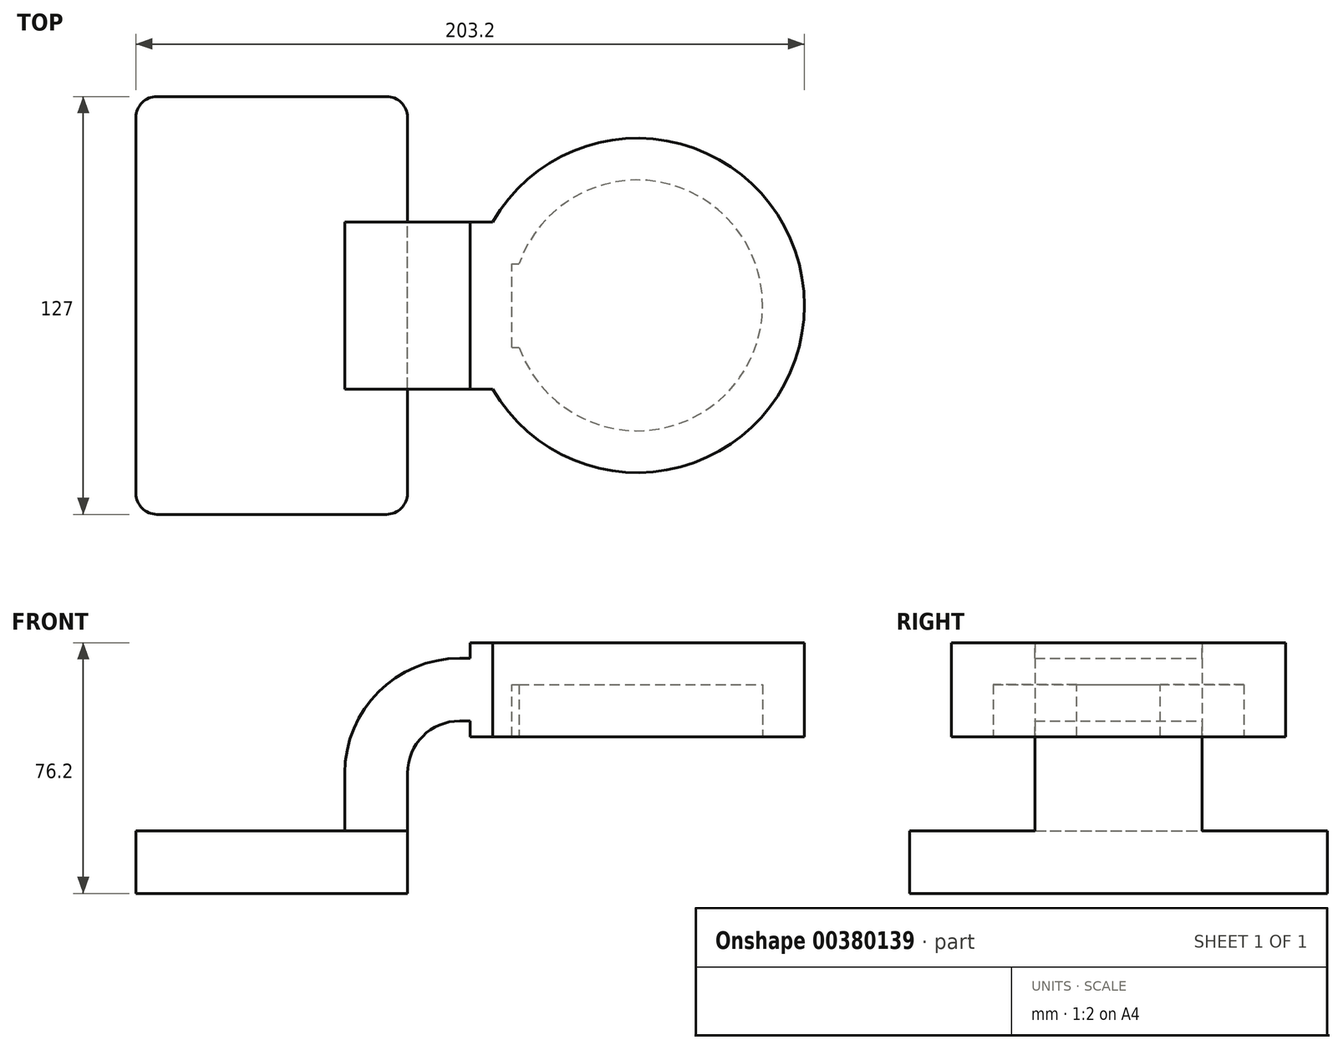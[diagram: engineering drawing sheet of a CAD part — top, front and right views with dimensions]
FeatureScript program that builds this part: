
annotation { "Feature Type Name" : "Feature", "Feature Type Description" : "" }
export const myFeature = defineFeature(function(context is Context, id is Id, definition is map)
    precondition{}
    {
        {
            var Q0;
            Q0=qCreatedBy(makeId("Front.planeOp"),FACE);
            var sketch = newSketch(context, id + "F0", { "sketchPlane" : qUnion([Q0])});
            skLineSegment(sketch, "E0.bottom", {"start": v(-41.28, 9.52) * mm, "end": v(41.27, 9.53) * mm});
            skLineSegment(sketch, "E0.top", {"start": v(-41.28, -9.53) * mm, "end": v(41.28, -9.53) * mm});
            skLineSegment(sketch, "E0.left", {"start": v(-41.28, 9.52) * mm, "end": v(-41.28, -9.53) * mm});
            skLineSegment(sketch, "E0.right", {"start": v(41.27, 9.53) * mm, "end": v(41.28, -9.52) * mm});
            skPoint(sketch, "E0.middle", {"position": v(0, 0) * mm});
            skLineSegment(sketch, "E1.bottom", {"start": v(60.32, 38.1) * mm, "end": v(111.12, 38.1) * mm});
            skLineSegment(sketch, "E1.top", {"start": v(60.32, 66.67) * mm, "end": v(111.12, 66.67) * mm});
            skLineSegment(sketch, "E1.left", {"start": v(60.32, 38.1) * mm, "end": v(60.32, 66.67) * mm});
            skLineSegment(sketch, "E1.right", {"start": v(111.12, 38.1) * mm, "end": v(111.12, 66.67) * mm});
            skPoint(sketch, "E1.middle", {"position": v(85.72, 52.39) * mm});
            skLineSegment(sketch, "E2", {"start": v(41.27, 9.53) * mm, "end": v(41.27, 27) * mm});
            skArc(sketch, "E3", {"start": v(41.27, 27) * mm, "mid": v(45.92, 38.23) * mm, "end": v(57.15, 42.88) * mm});
            skLineSegment(sketch, "E4", {"start": v(57.15, 42.88) * mm, "end": v(85.89, 42.88) * mm});
            skLineSegment(sketch, "E5.0", {"start": v(57.15, 61.93) * mm, "end": v(85.04, 61.93) * mm});
            skArc(sketch, "E5.1", {"start": v(22.22, 27) * mm, "mid": v(32.45, 51.7) * mm, "end": v(57.15, 61.93) * mm});
            skLineSegment(sketch, "E5.2", {"start": v(22.22, 9.53) * mm, "end": v(22.22, 27) * mm});
            skFitSpline(sketch, "E6", {"points": [v(-41.28, 9.52) * mm, v(57.15, 61.93) * mm], "startDerivative": vector(19.23, 63.9) * mm, "endDerivative": vector(202.06, -20.22) * mm});
            skSolve(sketch);
        }
        {
            var Q0;
            Q0=makeQuery(id+"F0.imprint","IMPRINT",FACE,{"disambiguationData":[TD([[makeQuery(id+"F0.imprint","IMPRINT",EDGE,{"derivedFrom":sQuery(id+"F0.wireOp",EDGE,"E0.top")}),1.0]])]});
            extrude(context, id + "F1", {"entities" : qUnion([Q0]), "depth" : 127 * mm, "symmetric" : true});
        }
        {
            var Q0;
            {var subQ1=sQuery(id+"F0.wireOp",EDGE,"E2");Q0=makeQuery(id+"F0.imprint","IMPRINT",FACE,{"disambiguationData":[TD([[makeQuery(id+"F0.imprint","IMPRINT",EDGE,{"derivedFrom":subQ1}),1.0]])]});}
            var Q1;
            {var subQ3=sQuery(id+"F0.wireOp",EDGE,"E1.bottom");Q1=makeQuery(id+"F0.imprint","IMPRINT",FACE,{"disambiguationData":[TD([[makeQuery(id+"F0.imprint","IMPRINT",EDGE,{"derivedFrom":subQ3}),1.0]])]});}
            extrude(context, id + "F2", {"entities" : qUnion([Q0, Q1]), "operationType" : NewBodyOperationType.ADD, "depth" : 50.8 * mm, "symmetric" : true});
        }
        {
            var Q0;
            Q0=makeQuery(id+"F0.imprint","IMPRINT",FACE,{"disambiguationData":[TD([[makeQuery(id+"F0.imprint","IMPRINT",EDGE,{"derivedFrom":sQuery(id+"F0.wireOp",EDGE,"E5.1")}),1.0]])]});
            extrude(context, id + "F3", {"entities" : qUnion([Q0]), "operationType" : NewBodyOperationType.ADD, "depth" : 15.88 * mm, "symmetric" : true});
        }
        {
            var Q0;
            {var subQ3=sQuery(id+"F0.wireOp",EDGE,"E1.bottom");Q0=makeQuery(id+"F0.imprint","IMPRINT",FACE,{"disambiguationData":[TD([[makeQuery(id+"F0.imprint","IMPRINT",EDGE,{"derivedFrom":subQ3}),1.0]])]});}
            var Q1;
            Q1=sQuery(id+"F0.wireOp",EDGE,"E1.right");
            revolve(context, id + "F4", {"operationType" : NewBodyOperationType.ADD, "entities" : qUnion([Q0]), "axis" : qUnion([Q1]), "revolveType" : RevolveType.FULL});
        }
        {
            var Q0;
            Q0=makeQuery(id+"F1.opExtrude","CAP_EDGE",EDGE,{"disambiguationData":[OSD([sQuery(id+"F0.wireOp",EDGE,"E0.left")])],"isStart":false});
            var Q1;
            Q1=makeQuery(id+"F1.opExtrude","CAP_EDGE",EDGE,{"disambiguationData":[OSD([sQuery(id+"F0.wireOp",EDGE,"E0.right")])],"isStart":false});
            var Q2;
            Q2=makeQuery(id+"F1.opExtrude","CAP_EDGE",EDGE,{"disambiguationData":[OSD([sQuery(id+"F0.wireOp",EDGE,"E0.right")])],"isStart":true});
            var Q3;
            Q3=makeQuery(id+"F1.opExtrude","CAP_EDGE",EDGE,{"disambiguationData":[OSD([sQuery(id+"F0.wireOp",EDGE,"E0.left")])],"isStart":true});
            fillet(context, id + "F5", {"entities" : qUnion([Q0, Q1, Q2, Q3]), "radius" : 6.35 * mm, "tangentPropagation" : true, "allowEdgeOverflow" : false});
        }
        {
            var Q0;
            {var subQ0=sQuery(id+"F0.wireOp",EDGE,"E1.bottom");Q0=makeQuery(id+"F4.boolean.opBoolean","MERGE",FACE,{"derivedFrom":[makeQuery(id+"F2.opExtrude","SWEPT_FACE",FACE,{"disambiguationData":[OSD([subQ0])]}),makeQuery(id+"F4.opRevolve","SWEPT_FACE",FACE,{"disambiguationData":[OSD([subQ0])]})]});}
            var Q1;
            Q1=makeQuery(id+"F1.opExtrude","SWEPT_FACE",FACE,{"disambiguationData":[OSD([sQuery(id+"F0.wireOp",EDGE,"E0.top")])]});
            shell(context, id + "F6", {"entities" : qUnion([Q0, Q1]), "thickness" : 12.7 * mm});
        }
    });
